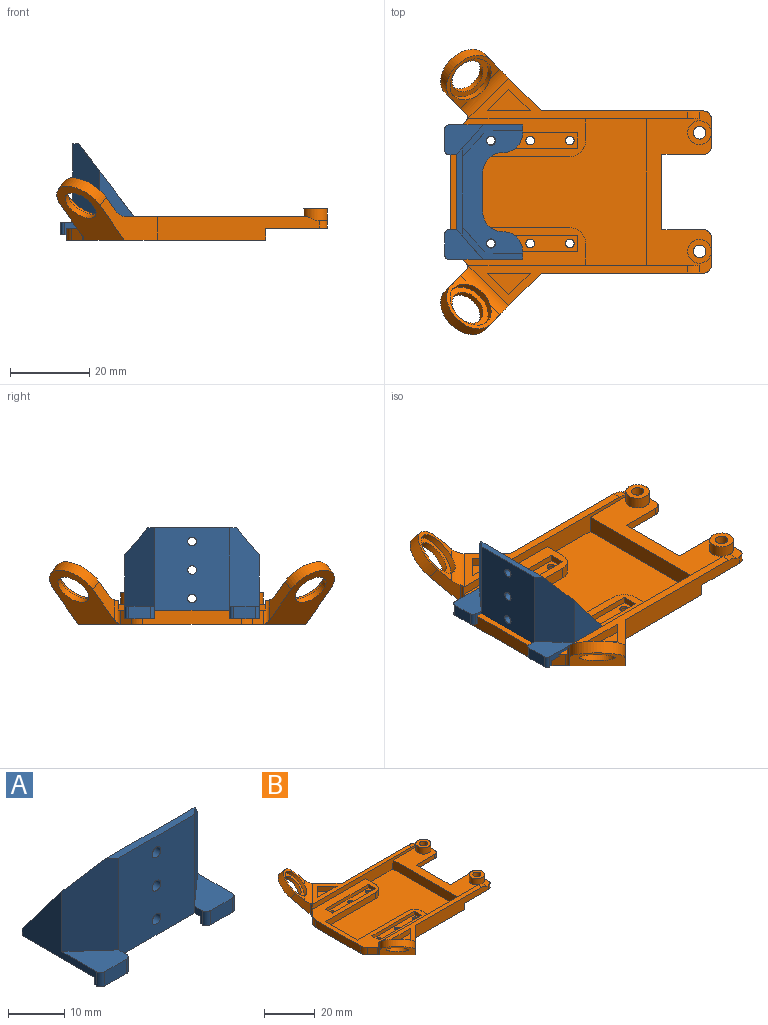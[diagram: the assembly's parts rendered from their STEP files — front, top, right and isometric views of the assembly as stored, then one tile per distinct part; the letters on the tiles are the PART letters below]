
ASSEMBLY  parts=2 mates=1
PART A: 47 faces, bbox 34x19.7x23 mm
  f0: plane 34x18.2mm, normal (0,0,-1), area 365.6mm2, adj f8,f9,f10,f11,f13,f15,f16,f17
  f1: plane 19.9x7.5mm, normal (0.67,-0.75,0), area 173.6mm2, adj f10,f13,f14,f22,f34
  f2: plane 19.9x7.5mm, normal (-0.67,-0.75,0), area 173.6mm2, adj f9,f13,f14,f23,f31
  f3: plane 31x15.2mm, normal (0,0,1), area 222.3mm2, adj f4,f5,f6,f7,f8,f11,f12,f15
  f4: plane 12.21x9.33mm, normal (-1,0,0), area 57mm2, adj f3,f5,f22
  f5: plane 19.9x6.57mm, normal (-0.67,0.75,0), area 141.5mm2, adj f3,f4,f12,f22
  f6: plane 19.9x6.57mm, normal (0.67,0.75,0), area 141.5mm2, adj f3,f7,f12,f23
  f7: plane 12.21x9.33mm, normal (1,0,0), area 57mm2, adj f3,f6,f23
  f8: plane 2x1.5mm, normal (0,1,0), area 3mm2, adj f0,f3,f9,f23,f46
  f9: plane 18.7x16.19mm, normal (-1,0,0), area 94.3mm2, adj f0,f2,f8,f23,f31,f35,f36,f41
  f10: plane 18.7x16.19mm, normal (1,0,0), area 94.3mm2, adj f0,f1,f11,f22,f34,f37,f38,f39
  f11: plane 2x1.5mm, normal (0,1,0), area 3mm2, adj f0,f3,f10,f22,f43
  f12: plane 19.9x17.86mm, normal (0,1,0), area 343.9mm2, adj f3,f5,f6,f14,f26,f27,f28
  f13: plane 21.4x19mm, normal (0,-1,0), area 395.2mm2, adj f0,f1,f2,f14,f26,f27,f28,f30
  f14: plane 22.36x1.5mm, normal (0,0,1), area 31mm2, adj f1,f2,f12,f13,f22,f23
  f15: plane 1.5x0.1mm, normal (-1,0,0), area 0.2mm2, adj f0,f3,f43,f44
  f16: plane 10x1.5mm, normal (0,1,0), area 15mm2, adj f0,f3,f44,f45
  f17: plane 1.5x0.1mm, normal (1,0,0), area 0.2mm2, adj f0,f3,f45,f46
  f18: cylinder r=1.9mm len=3.8mm, axis (0,0,1), area 19.1mm2, adj f0,f19
  f19: plane 3.8x3.8mm, normal (0,0,-1), area 7.2mm2, adj f18,f25
  f20: cylinder r=1.9mm len=3.8mm, axis (0,0,1), area 19.1mm2, adj f0,f21
  f21: plane 3.8x3.8mm, normal (0,0,-1), area 7.2mm2, adj f20,f24
  f22: plane 19.9x15.2mm, normal (0,0.79,0.61), area 44.4mm2, adj f1,f4,f5,f10,f11,f14
  f23: plane 19.9x15.2mm, normal (0,0.79,0.61), area 44.4mm2, adj f2,f6,f7,f8,f9,f14
  f24: cylinder r=1.15mm len=3.1mm, axis (0,0,-1), area 22.4mm2, adj f3,f21
  f25: cylinder r=1.15mm len=3.1mm, axis (0,0,-1), area 22.4mm2, adj f3,f19
  f26: cylinder r=1.1mm len=2.2mm, axis (0,-1,0), area 10.4mm2, adj f12,f13
  f27: cylinder r=1.1mm len=2.2mm, axis (0,-1,0), area 10.4mm2, adj f12,f13
  f28: cylinder r=1.1mm len=2.2mm, axis (0,-1,0), area 10.4mm2, adj f12,f13
  f29: plane 5.5x3.1mm, normal (0,-1,0), area 17.1mm2, adj f31,f36,f41,f42
  f30: plane 3.1x2mm, normal (1,0,0), area 3.8mm2, adj f0,f13,f31,f35,f36,f42
  f31: plane 9.7x7.5mm, normal (0,0,1), area 47.2mm2, adj f2,f9,f29,f30,f41,f42
  f32: plane 5.5x3.1mm, normal (0,-1,0), area 17.1mm2, adj f34,f38,f39,f40
  f33: plane 3.1x2mm, normal (-1,0,0), area 3.8mm2, adj f0,f13,f34,f37,f38,f40
  f34: plane 9.7x7.5mm, normal (0,0,1), area 47.2mm2, adj f1,f10,f32,f33,f39,f40
  f35: plane 7.5x1.6mm, normal (0,1,0), area 12mm2, adj f0,f9,f30,f36
  f36: plane 7.5x1.5mm, normal (0,0,-1), area 10.8mm2, adj f9,f29,f30,f35,f41,f42
  f37: plane 7.5x1.6mm, normal (0,1,0), area 12mm2, adj f0,f10,f33,f38
  f38: plane 7.5x1.5mm, normal (0,0,-1), area 10.8mm2, adj f10,f32,f33,f37,f39,f40
  f39: cylinder r=1mm len=3.1mm, axis (0,0,1), area 4.9mm2, adj f10,f32,f34,f38
  f40: cylinder r=1mm len=3.1mm, axis (0,0,-1), area 4.9mm2, adj f32,f33,f34,f38
  f41: cylinder r=1mm len=3.1mm, axis (0,0,1), area 4.9mm2, adj f9,f29,f31,f36
  f42: cylinder r=1mm len=3.1mm, axis (0,0,-1), area 4.9mm2, adj f29,f30,f31,f36
  f43: cylinder r=5mm len=5mm, axis (0,0,-1), area 11.8mm2, adj f0,f3,f11,f15
  f44: cylinder r=5mm len=5mm, axis (0,0,1), area 11.8mm2, adj f0,f3,f15,f16
  f45: cylinder r=5mm len=5mm, axis (0,0,-1), area 11.8mm2, adj f0,f3,f16,f17
  f46: cylinder r=5mm len=5mm, axis (0,0,-1), area 11.8mm2, adj f0,f3,f8,f17
PART B: 128 faces, bbox 68.5x72.1x15.8 mm
  f0: plane 37x34.1mm, normal (0,0,1), area 465.5mm2, adj f15,f16,f26,f39,f40,f106,f107,f108
  f1: plane 57.56x50.35mm, normal (0,0,-1), area 2083.9mm2, adj f11,f15,f16,f20,f21,f26,f27,f29
  f2: cylinder r=1.1mm len=2.2mm, axis (0,0,-1), area 4.8mm2, adj f99,f111
  f3: cylinder r=1.1mm len=2.2mm, axis (0,0,-1), area 4.8mm2, adj f92,f111
  f4: cylinder r=1.1mm len=2.2mm, axis (0,0,-1), area 4.8mm2, adj f91,f110
  f5: cylinder r=1.1mm len=2.2mm, axis (0,0,-1), area 4.8mm2, adj f84,f110
  f6: cylinder r=1.1mm len=2.2mm, axis (0,0,-1), area 4.8mm2, adj f71,f111
  f7: cylinder r=1.1mm len=2.2mm, axis (0,0,-1), area 4.8mm2, adj f70,f110
  f8: plane 41x15.55mm, normal (0,0,-1), area 380.5mm2, adj f9,f11,f12,f13,f14,f28,f29,f37
  f9: plane 7x2mm, normal (1,0,0), area 14mm2, adj f8,f49,f62,f63
  f10: plane 55.56x10.28mm, normal (0,0,1), area 147.9mm2, adj f21,f29,f40,f45,f46,f47,f56,f58
  f11: plane 41x6mm, normal (0,1,0), area 203.4mm2, adj f1,f8,f17,f27,f37,f49,f57,f60
  f12: plane 10.5x2mm, normal (0,-1,0), area 21mm2, adj f8,f13,f49,f61
  f13: plane 19x2mm, normal (1,0,0), area 38mm2, adj f8,f12,f14,f49
  f14: plane 10.5x2mm, normal (0,1,0), area 21mm2, adj f8,f13,f49,f62
  f15: plane 3.6x2.84mm, normal (-0.71,-0.71,0), area 14.5mm2, adj f0,f1,f124,f126
  f16: plane 25x3.6mm, normal (-1,0,0), area 90mm2, adj f0,f1,f124,f125
  f17: plane 55.56x10.28mm, normal (0,0,1), area 147.9mm2, adj f11,f27,f39,f41,f42,f43,f57,f59
  f18: cylinder r=4.5mm len=8.54mm, axis (0.5,0.5,0.71), area 42.4mm2, adj f20,f24
  f19: plane 13.41x13.41mm, normal (0.5,0.5,0.71), area 37mm2, adj f21,f22,f23,f25,f58
  f20: plane 17.89x17.18mm, normal (-0.5,-0.5,-0.71), area 186.5mm2, adj f1,f18,f21,f22,f23,f126
  f21: plane 14.45x14.45mm, normal (0.71,-0.71,0), area 104.8mm2, adj f1,f10,f19,f20,f23,f29,f58
  f22: plane 9.85x5.46mm, normal (-0.71,0.71,0), area 29mm2, adj f19,f20,f23,f58,f126
  f23: cylinder r=7mm len=12.51mm, axis (0.5,0.5,0.71), area 66mm2, adj f19,f20,f21,f22
  f24: plane 10.39x10.39mm, normal (0.5,0.5,0.71), area 49.5mm2, adj f18,f25
  f25: cylinder r=6mm len=11.22mm, axis (0.5,0.5,0.71), area 57.1mm2, adj f19,f24,f58
  f26: plane 3.6x2.84mm, normal (-0.71,0.71,0), area 14.5mm2, adj f0,f1,f125,f127
  f27: plane 14.45x14.45mm, normal (0.71,0.71,0), area 104.8mm2, adj f1,f11,f17,f30,f33,f34,f59
  f28: plane 7x2mm, normal (1,0,0), area 14mm2, adj f8,f49,f60,f61
  f29: plane 41x6mm, normal (0,-1,0), area 203.4mm2, adj f1,f8,f10,f21,f37,f49,f56,f63
  f30: plane 13.41x13.41mm, normal (0.5,-0.5,0.71), area 37mm2, adj f27,f31,f34,f36,f59
  f31: plane 9.85x5.46mm, normal (-0.71,-0.71,0), area 29mm2, adj f30,f33,f34,f59,f127
  f32: cylinder r=4.5mm len=8.54mm, axis (0.5,-0.5,0.71), area 42.4mm2, adj f33,f35
  f33: plane 17.89x17.18mm, normal (-0.5,0.5,-0.71), area 186.5mm2, adj f1,f27,f31,f32,f34,f127
  f34: cylinder r=7mm len=12.51mm, axis (0.5,-0.5,0.71), area 66mm2, adj f27,f30,f31,f33
  f35: plane 10.39x10.39mm, normal (0.5,-0.5,0.71), area 49.5mm2, adj f32,f36
  f36: cylinder r=6mm len=11.22mm, axis (0.5,-0.5,0.71), area 57.1mm2, adj f30,f35,f59
  f37: plane 41x3mm, normal (1,0,0), area 123mm2, adj f1,f8,f11,f29
  f38: plane 37x4.4mm, normal (-1,0,0), area 162.8mm2, adj f39,f40,f49,f121
  f39: plane 58.67x5.41mm, normal (0,-1,0), area 166.8mm2, adj f0,f17,f38,f49,f57,f59,f120,f121
  f40: plane 58.67x5.41mm, normal (0,1,0), area 166.8mm2, adj f0,f10,f38,f49,f56,f58,f116,f121
  f41: plane 5.45x5.45mm, normal (0.71,-0.71,0), area 18.5mm2, adj f17,f42,f43,f44
  f42: plane 10.9x2.4mm, normal (0,1,0), area 26.2mm2, adj f17,f41,f43,f44
  f43: plane 5.45x5.45mm, normal (-0.71,-0.71,0), area 18.5mm2, adj f17,f41,f42,f44
  f44: plane 10.9x5.45mm, normal (0,0,1), area 29.7mm2, adj f41,f42,f43
  f45: plane 10.9x2.4mm, normal (0,-1,0), area 26.2mm2, adj f10,f46,f47,f48
  f46: plane 5.45x5.45mm, normal (0.71,0.71,0), area 18.5mm2, adj f10,f45,f47,f48
  f47: plane 5.45x5.45mm, normal (-0.71,0.71,0), area 18.5mm2, adj f10,f45,f46,f48
  f48: plane 10.9x5.45mm, normal (0,0,1), area 29.7mm2, adj f45,f46,f47
  f49: plane 41x16.5mm, normal (0,0,1), area 325mm2, adj f9,f11,f12,f13,f14,f28,f29,f38
  f50: cylinder r=3mm len=6mm, axis (0,0,-1), area 56.5mm2, adj f49,f51
  f51: plane 6x6mm, normal (0,0,1), area 20.2mm2, adj f50,f55
  f52: cylinder r=3mm len=6mm, axis (0,0,-1), area 56.5mm2, adj f49,f53
  f53: plane 6x6mm, normal (0,0,1), area 20.2mm2, adj f52,f54
  f54: cylinder r=1.6mm len=5mm, axis (0,0,1), area 50.3mm2, adj f8,f53
  f55: cylinder r=1.6mm len=5mm, axis (0,0,1), area 50.3mm2, adj f8,f51
  f56: cylinder r=5mm len=3mm, axis (0,1,0), area 6.4mm2, adj f10,f29,f40,f49
  f57: cylinder r=5mm len=3mm, axis (0,-1,0), area 6.4mm2, adj f11,f17,f39,f49
  f58: cylinder r=5mm len=12.6mm, axis (0.71,-0.71,0), area 44.7mm2, adj f10,f19,f21,f22,f25,f40,f126
  f59: cylinder r=5mm len=12.6mm, axis (0.71,0.71,0), area 44.7mm2, adj f17,f27,f30,f31,f36,f39,f127
  f60: cylinder r=2mm len=2mm, axis (0,0,-1), area 6.3mm2, adj f8,f11,f28,f49
  f61: cylinder r=2mm len=2mm, axis (0,0,-1), area 6.3mm2, adj f8,f12,f28,f49
  f62: cylinder r=2mm len=2mm, axis (0,0,-1), area 6.3mm2, adj f8,f9,f14,f49
  f63: cylinder r=2mm len=2mm, axis (0,0,-1), area 6.3mm2, adj f8,f9,f29,f49
  f64: plane 1.92x1.3mm, normal (-0.5,-0.87,0), area 2.9mm2, adj f1,f65,f69,f70
  f65: plane 2.22x1.3mm, normal (-1,0,0), area 2.9mm2, adj f1,f64,f66,f70
  f66: plane 1.92x1.3mm, normal (-0.5,0.87,0), area 2.9mm2, adj f1,f65,f67,f70
  f67: plane 1.92x1.3mm, normal (0.5,0.87,0), area 2.9mm2, adj f1,f66,f68,f70
  f68: plane 2.22x1.3mm, normal (1,0,0), area 2.9mm2, adj f1,f67,f69,f70
  f69: plane 1.92x1.3mm, normal (0.5,-0.87,0), area 2.9mm2, adj f1,f64,f68,f70
  f70: plane 4.43x3.84mm, normal (0,0,-1), area 9mm2, adj f7,f64,f65,f66,f67,f68,f69
  f71: plane 4.43x3.84mm, normal (0,0,-1), area 9mm2, adj f6,f72,f73,f74,f75,f76,f77
  f72: plane 1.92x1.3mm, normal (0.5,-0.87,0), area 2.9mm2, adj f1,f71,f73,f77
  f73: plane 1.92x1.3mm, normal (-0.5,-0.87,0), area 2.9mm2, adj f1,f71,f72,f74
  f74: plane 2.22x1.3mm, normal (-1,0,0), area 2.9mm2, adj f1,f71,f73,f75
  f75: plane 1.92x1.3mm, normal (-0.5,0.87,0), area 2.9mm2, adj f1,f71,f74,f76
  f76: plane 1.92x1.3mm, normal (0.5,0.87,0), area 2.9mm2, adj f1,f71,f75,f77
  f77: plane 2.22x1.3mm, normal (1,0,0), area 2.9mm2, adj f1,f71,f72,f76
  f78: plane 1.92x1.3mm, normal (-0.5,-0.87,0), area 2.9mm2, adj f1,f79,f83,f84
  f79: plane 2.22x1.3mm, normal (-1,0,0), area 2.9mm2, adj f1,f78,f80,f84
  f80: plane 1.92x1.3mm, normal (-0.5,0.87,0), area 2.9mm2, adj f1,f79,f81,f84
  f81: plane 1.92x1.3mm, normal (0.5,0.87,0), area 2.9mm2, adj f1,f80,f82,f84
  f82: plane 2.22x1.3mm, normal (1,0,0), area 2.9mm2, adj f1,f81,f83,f84
  f83: plane 1.92x1.3mm, normal (0.5,-0.87,0), area 2.9mm2, adj f1,f78,f82,f84
  f84: plane 4.43x3.84mm, normal (0,0,-1), area 9mm2, adj f5,f78,f79,f80,f81,f82,f83
  f85: plane 1.92x1.3mm, normal (0.5,-0.87,0), area 2.9mm2, adj f1,f86,f90,f91
  f86: plane 1.92x1.3mm, normal (-0.5,-0.87,0), area 2.9mm2, adj f1,f85,f87,f91
  f87: plane 2.22x1.3mm, normal (-1,0,0), area 2.9mm2, adj f1,f86,f88,f91
  f88: plane 1.92x1.3mm, normal (-0.5,0.87,0), area 2.9mm2, adj f1,f87,f89,f91
  f89: plane 1.92x1.3mm, normal (0.5,0.87,0), area 2.9mm2, adj f1,f88,f90,f91
  f90: plane 2.22x1.3mm, normal (1,0,0), area 2.9mm2, adj f1,f85,f89,f91
  f91: plane 4.43x3.84mm, normal (0,0,-1), area 9mm2, adj f4,f85,f86,f87,f88,f89,f90
  f92: plane 4.43x3.84mm, normal (0,0,-1), area 9mm2, adj f3,f93,f94,f95,f96,f97,f98
  f93: plane 1.92x1.3mm, normal (0.5,-0.87,0), area 2.9mm2, adj f1,f92,f94,f98
  f94: plane 1.92x1.3mm, normal (-0.5,-0.87,0), area 2.9mm2, adj f1,f92,f93,f95
  f95: plane 2.22x1.3mm, normal (-1,0,0), area 2.9mm2, adj f1,f92,f94,f96
  f96: plane 1.92x1.3mm, normal (-0.5,0.87,0), area 2.9mm2, adj f1,f92,f95,f97
  f97: plane 1.92x1.3mm, normal (0.5,0.87,0), area 2.9mm2, adj f1,f92,f96,f98
  f98: plane 2.22x1.3mm, normal (1,0,0), area 2.9mm2, adj f1,f92,f93,f97
  f99: plane 4.43x3.84mm, normal (0,0,-1), area 9mm2, adj f2,f100,f101,f102,f103,f104,f105
  f100: plane 1.92x1.3mm, normal (-0.5,-0.87,0), area 2.9mm2, adj f1,f99,f101,f105
  f101: plane 2.22x1.3mm, normal (-1,0,0), area 2.9mm2, adj f1,f99,f100,f102
  f102: plane 1.92x1.3mm, normal (-0.5,0.87,0), area 2.9mm2, adj f1,f99,f101,f103
  f103: plane 1.92x1.3mm, normal (0.5,0.87,0), area 2.9mm2, adj f1,f99,f102,f104
  f104: plane 2.22x1.3mm, normal (1,0,0), area 2.9mm2, adj f1,f99,f103,f105
  f105: plane 1.92x1.3mm, normal (0.5,-0.87,0), area 2.9mm2, adj f1,f99,f100,f104
  f106: plane 24x1.6mm, normal (0,1,0), area 38.4mm2, adj f0,f107,f109,f110
  f107: plane 4x1.6mm, normal (1,0,0), area 6.4mm2, adj f0,f106,f108,f110
  f108: plane 24x1.6mm, normal (0,-1,0), area 38.4mm2, adj f0,f107,f109,f110
  f109: plane 4x1.6mm, normal (-1,0,0), area 6.4mm2, adj f0,f106,f108,f110
  f110: plane 24x4mm, normal (0,0,1), area 84.6mm2, adj f4,f5,f7,f106,f107,f108,f109
  f111: plane 24x4mm, normal (0,0,1), area 84.6mm2, adj f2,f3,f6,f112,f113,f114,f115
  f112: plane 4x1.6mm, normal (1,0,0), area 6.4mm2, adj f0,f111,f113,f114
  f113: plane 24x1.6mm, normal (0,1,0), area 38.4mm2, adj f0,f111,f112,f115
  f114: plane 24x1.6mm, normal (0,-1,0), area 38.4mm2, adj f0,f111,f112,f115
  f115: plane 4x1.6mm, normal (-1,0,0), area 6.4mm2, adj f0,f111,f113,f114
  f116: plane 5.5x3mm, normal (1,0,0), area 16.5mm2, adj f0,f40,f121,f122
  f117: plane 28.1x3mm, normal (0,1,0), area 84.3mm2, adj f0,f118,f121,f122
  f118: plane 18x3mm, normal (1,0,0), area 54mm2, adj f0,f117,f119,f121
  f119: plane 28.1x3mm, normal (0,-1,0), area 84.3mm2, adj f0,f118,f121,f123
  f120: plane 5.5x3mm, normal (1,0,0), area 16.5mm2, adj f0,f39,f121,f123
  f121: plane 47.4x37mm, normal (0,0,1), area 1150.8mm2, adj f38,f39,f40,f116,f117,f118,f119,f120
  f122: cylinder r=4mm len=4mm, axis (0,0,1), area 18.8mm2, adj f0,f116,f117,f121
  f123: cylinder r=4mm len=4mm, axis (0,0,1), area 18.8mm2, adj f0,f119,f120,f121
  f124: cylinder r=4mm len=3.6mm, axis (0,0,-1), area 11.3mm2, adj f0,f1,f15,f16
  f125: cylinder r=4mm len=3.6mm, axis (0,0,1), area 11.3mm2, adj f0,f1,f16,f26
  f126: cylinder r=1mm len=6.17mm, axis (0,0,-1), area 8mm2, adj f0,f15,f20,f22,f40,f58
  f127: cylinder r=1mm len=6.17mm, axis (0,0,-1), area 8mm2, adj f0,f26,f31,f33,f39,f59
PLACE A rot(axis=(0,0,-1),90deg) t=(-34.72,4.59,0.85)mm
PLACE B t=(34.98,4.61,-6.15)mm fixed
MATE planar A.f35 <-> B.f16  axis (1,0,0) through (-42.92,21.59,0.05)mm
